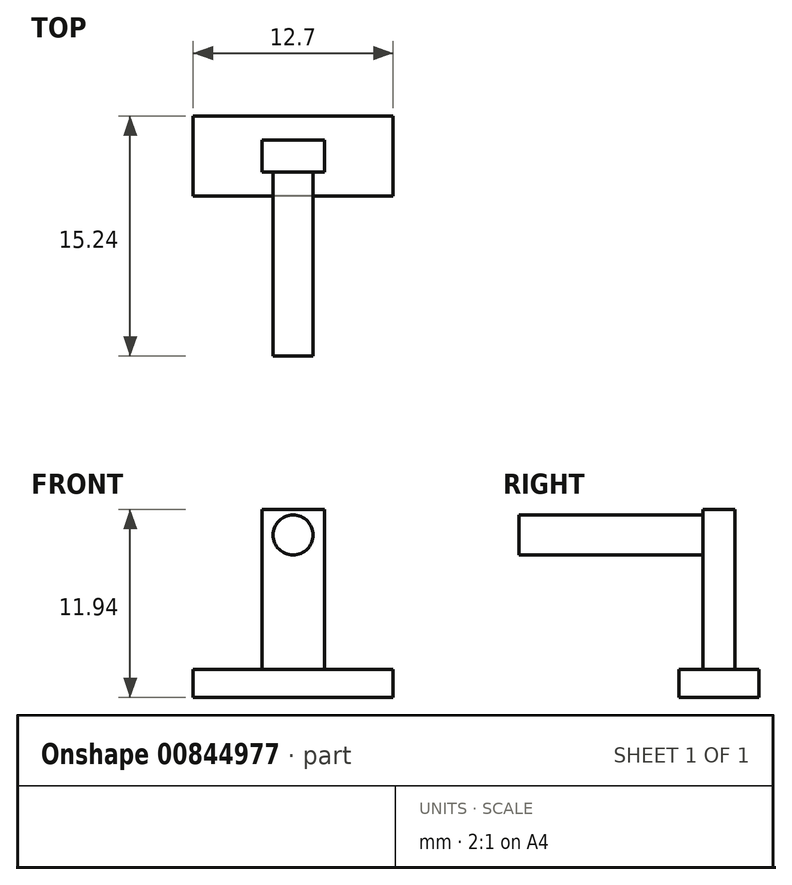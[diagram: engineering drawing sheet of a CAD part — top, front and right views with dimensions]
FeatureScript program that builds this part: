
annotation { "Feature Type Name" : "Feature", "Feature Type Description" : "" }
export const myFeature = defineFeature(function(context is Context, id is Id, definition is map)
    precondition{}
    {
        {
            var Q0;
            Q0=qCreatedBy(makeId("Top.planeOp"),FACE);
            var sketch = newSketch(context, id + "F0", { "sketchPlane" : qUnion([Q0])});
            skLineSegment(sketch, "E0.bottom", {"start": v(6.35, -2.54) * mm, "end": v(-6.35, -2.54) * mm});
            skLineSegment(sketch, "E0.top", {"start": v(6.35, 2.54) * mm, "end": v(-6.35, 2.54) * mm});
            skLineSegment(sketch, "E0.left", {"start": v(6.35, -2.54) * mm, "end": v(6.35, 2.54) * mm});
            skLineSegment(sketch, "E0.right", {"start": v(-6.35, -2.54) * mm, "end": v(-6.35, 2.54) * mm});
            skPoint(sketch, "E0.middle", {"position": v(0, 0) * mm});
            skSolve(sketch);
        }
        {
            var Q0;
            Q0=makeQuery(id+"F0.imprint","IMPRINT",FACE,{"disambiguationData":[TD([[makeQuery(id+"F0.imprint","IMPRINT",EDGE,{"derivedFrom":sQuery(id+"F0.wireOp",EDGE,"E0.bottom")}),-1.0]])]});
            extrude(context, id + "F1", {"entities" : qUnion([Q0]), "depth" : 1.78 * mm, "offsetDistance" : 25.4 * mm});
        }
        {
            var Q0;
            Q0=qCreatedBy(makeId("Top.planeOp"),FACE);
            cPlane(context, id + "F2", {"entities" : qUnion([Q0]), "cplaneType" : CPlaneType.OFFSET, "offset" : 1.78 * mm, "width" : 152.4 * mm, "height" : 152.4 * mm});
        }
        {
            var Q0;
            Q0=qCreatedBy(id+"F2.planeOp",FACE);
            var sketch = newSketch(context, id + "F3", { "sketchPlane" : qUnion([Q0])});
            skLineSegment(sketch, "E1.bottom", {"start": v(1.98, 1.02) * mm, "end": v(-1.98, 1.02) * mm});
            skLineSegment(sketch, "E1.top", {"start": v(1.98, -1.02) * mm, "end": v(-1.98, -1.02) * mm});
            skLineSegment(sketch, "E1.left", {"start": v(1.98, 1.02) * mm, "end": v(1.98, -1.02) * mm});
            skLineSegment(sketch, "E1.right", {"start": v(-1.98, 1.02) * mm, "end": v(-1.98, -1.02) * mm});
            skPoint(sketch, "E1.middle", {"position": v(0, 0) * mm});
            skSolve(sketch);
        }
        {
            var Q0;
            Q0 = qSketchRegion(id + "F3", true);
            extrude(context, id + "F4", {"entities" : qUnion([Q0]), "operationType" : NewBodyOperationType.ADD, "depth" : 10.16 * mm, "offsetDistance" : 25.4 * mm});
        }
        {
            var Q0;
            Q0=qCreatedBy(makeId("Front.planeOp"),FACE);
            var sketch = newSketch(context, id + "F5", { "sketchPlane" : qUnion([Q0])});
            skCircle(sketch, "E2", {"center": v(0, 10.32) * mm, "radius": 1.27 * mm});
            skSolve(sketch);
        }
        {
            var Q0;
            Q0 = qSketchRegion(id + "F5", true);
            extrude(context, id + "F6", {"entities" : qUnion([Q0]), "operationType" : NewBodyOperationType.ADD, "depth" : 12.7 * mm, "offsetDistance" : 25.4 * mm});
        }
    });
